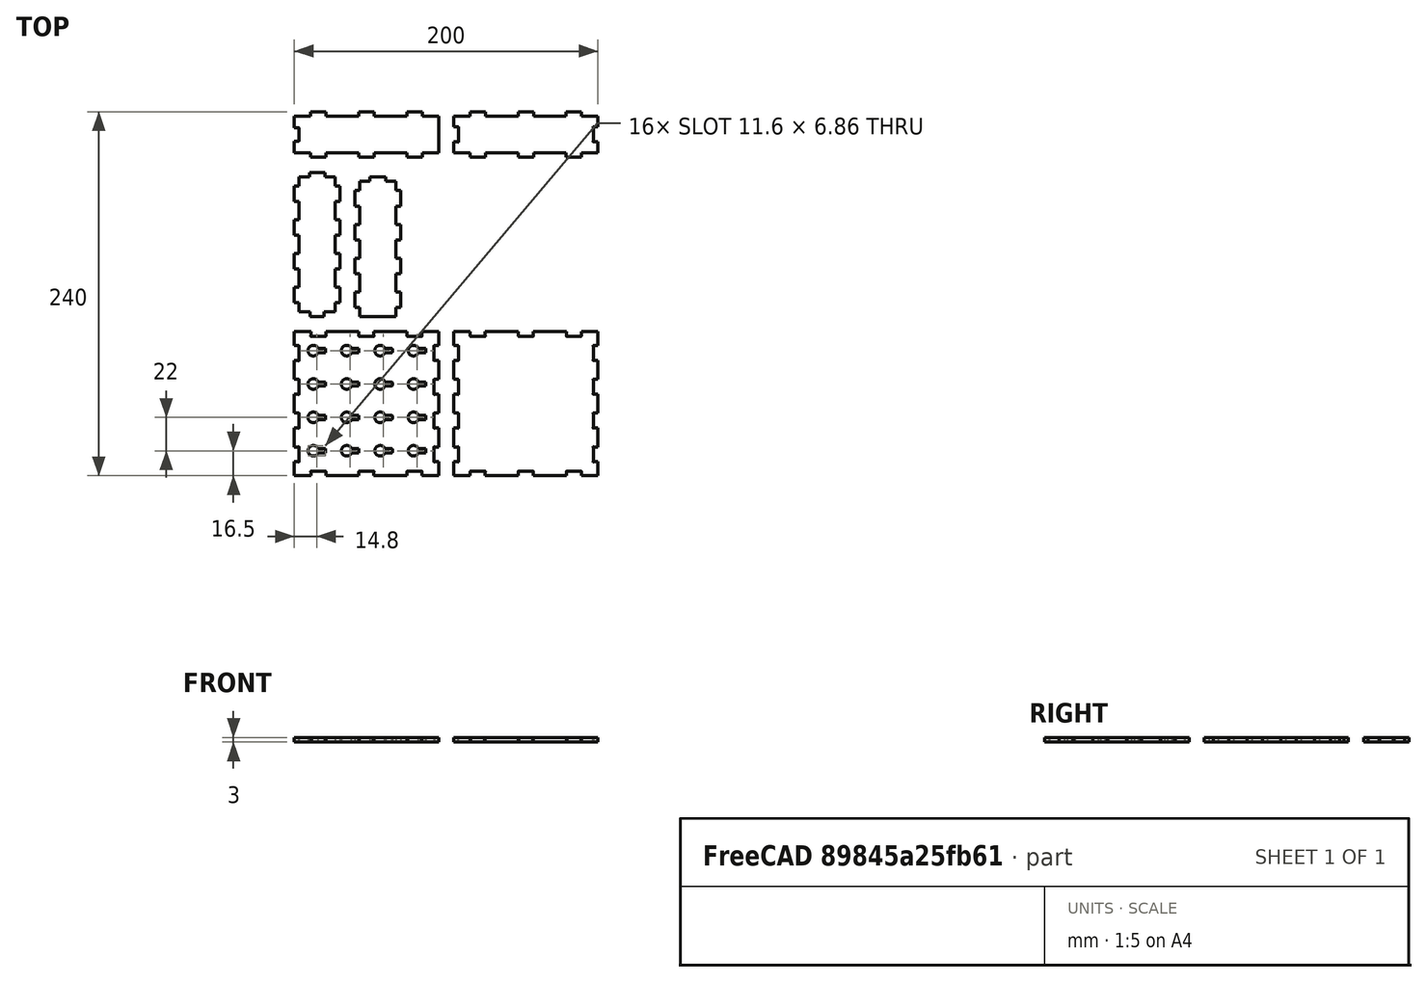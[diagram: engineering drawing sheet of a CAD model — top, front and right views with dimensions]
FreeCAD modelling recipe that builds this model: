
FCSTD DOCUMENT  (FreeCAD 0.20R)
Label: export_box6
License: All rights reserved
LicenseURL: http://en.wikipedia.org/wiki/All_rights_reserved
objects: Part::Feature×6, Part::Part2DObjectPython×6
note: 12 computed .brp shape members not serialized (recipe doc carries the construction recipe); baked Part::Feature solids carry a one-line shape summary decoded from their .brp

FEATURE [Part::Feature] test
  Placement = pos=(47.5,47.5,45) rot=(0,-1,0;3.14159rad)
  shape: bbox 95 x 95 x 3 mm, 154 faces (baked)
FEATURE [Part::Feature] test001
  Placement = pos=(152.5,47.5,18) rot=(0,-1,0;3.14159rad)
  shape: bbox 95 x 95 x 3 mm, 90 faces (baked)
FEATURE [Part::Feature] test002
  Placement = pos=(15,152.5,-14.5) rot=(0,1,0;1.5708rad)
  shape: bbox 30 x 95 x 3 mm, 46 faces (baked)
FEATURE [Part::Feature] test003
  Placement = pos=(55,149.5,77.5) rot=(0,1,0;1.5708rad)
  shape: bbox 30 x 92 x 3 mm, 42 faces (baked)
FEATURE [Part::Feature] test004
  Placement = pos=(47.5,225,-14.5) rot=(-1,0,0;1.5708rad)
  shape: bbox 95 x 30 x 3 mm, 36 faces (baked)
FEATURE [Part::Feature] test005
  Placement = pos=(152.5,225,77.5) rot=(-1,0,0;1.5708rad)
  shape: bbox 95 x 30 x 3 mm, 42 faces (baked)
FEATURE [Part::Part2DObjectPython] Shape2DView  # Draft 2D object (typed FeaturePython)
  AutoUpdate = true
  Base = -> test
  Clip = false
  FuseArch = false
  HiddenLines = false
  InPlace = true
  OnlySolids = false
  Projection = (0,0,1)
  ProjectionMode = 0
  SegmentLength = 0.05
  Tessellation = false
  VisibleOnly = false
FEATURE [Part::Part2DObjectPython] Shape2DView001  # Draft 2D object (typed FeaturePython)
  AutoUpdate = true
  Base = -> test001
  Clip = false
  FuseArch = false
  HiddenLines = false
  InPlace = true
  OnlySolids = false
  Projection = (0,0,1)
  ProjectionMode = 0
  SegmentLength = 0.05
  Tessellation = false
  VisibleOnly = false
FEATURE [Part::Part2DObjectPython] Shape2DView002  # Draft 2D object (typed FeaturePython)
  AutoUpdate = true
  Base = -> test002
  Clip = false
  FuseArch = false
  HiddenLines = false
  InPlace = true
  OnlySolids = false
  Projection = (0,0,1)
  ProjectionMode = 0
  SegmentLength = 0.05
  Tessellation = false
  VisibleOnly = false
FEATURE [Part::Part2DObjectPython] Shape2DView003  # Draft 2D object (typed FeaturePython)
  AutoUpdate = true
  Base = -> test003
  Clip = false
  FuseArch = false
  HiddenLines = false
  InPlace = true
  OnlySolids = false
  Projection = (0,0,1)
  ProjectionMode = 0
  SegmentLength = 0.05
  Tessellation = false
  VisibleOnly = false
FEATURE [Part::Part2DObjectPython] Shape2DView004  # Draft 2D object (typed FeaturePython)
  AutoUpdate = true
  Base = -> test004
  Clip = false
  FuseArch = false
  HiddenLines = false
  InPlace = true
  OnlySolids = false
  Projection = (0,0,1)
  ProjectionMode = 0
  SegmentLength = 0.05
  Tessellation = false
  VisibleOnly = false
FEATURE [Part::Part2DObjectPython] Shape2DView005  # Draft 2D object (typed FeaturePython)
  AutoUpdate = true
  Base = -> test005
  Clip = false
  FuseArch = false
  HiddenLines = false
  InPlace = true
  OnlySolids = false
  Projection = (0,0,1)
  ProjectionMode = 0
  SegmentLength = 0.05
  Tessellation = false
  VisibleOnly = false
